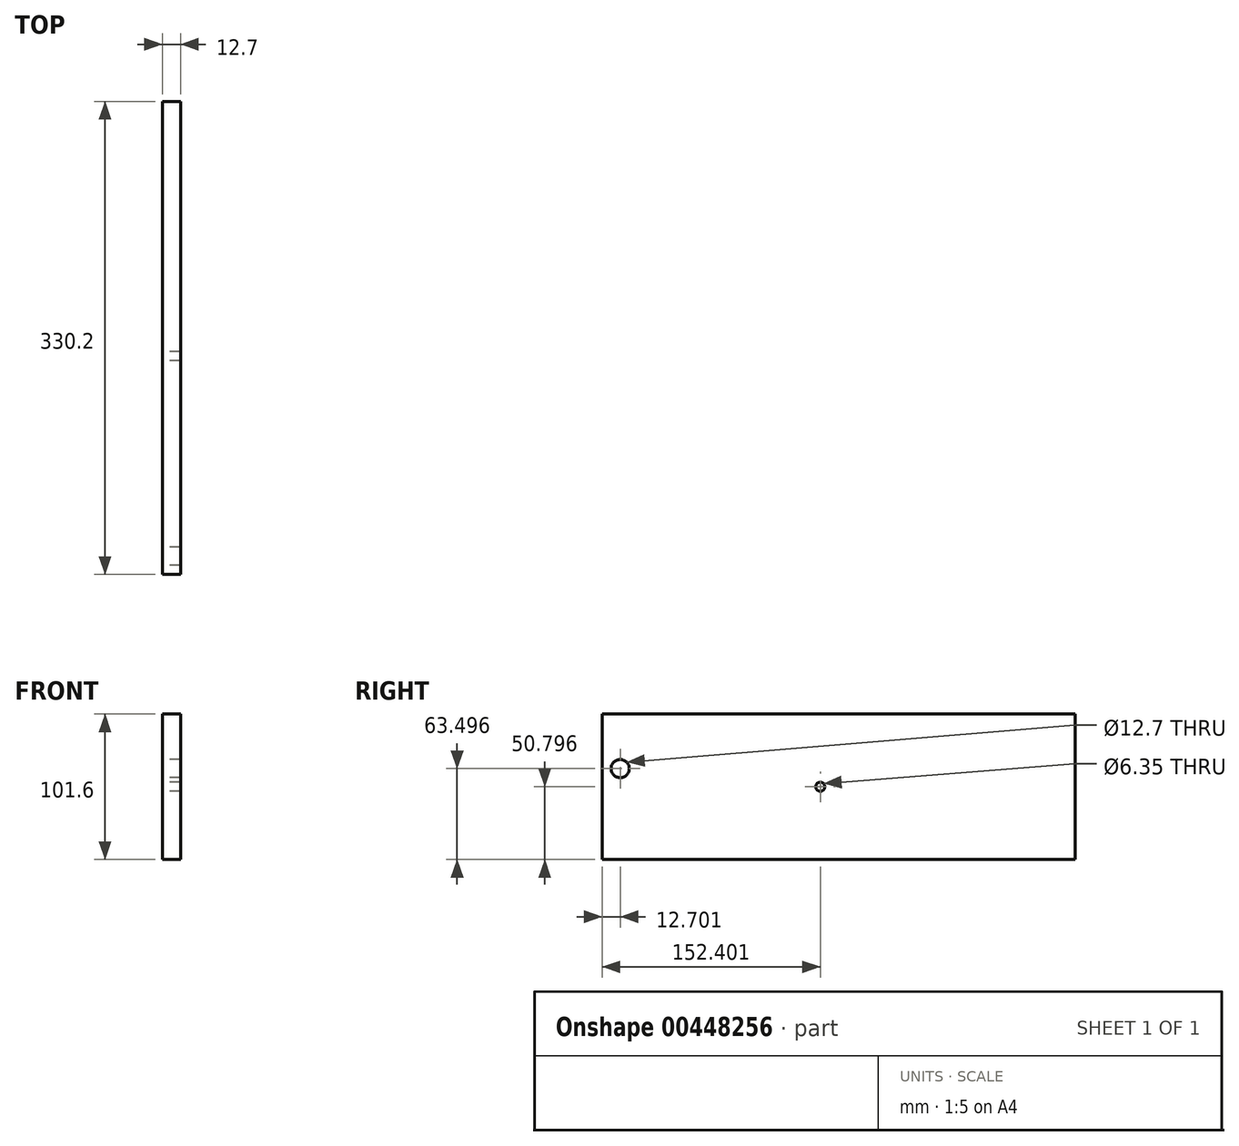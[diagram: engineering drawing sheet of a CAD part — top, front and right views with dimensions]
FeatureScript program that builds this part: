
annotation { "Feature Type Name" : "Feature", "Feature Type Description" : "" }
export const myFeature = defineFeature(function(context is Context, id is Id, definition is map)
    precondition{}
    {
        {
            var Q0;
            Q0=qCreatedBy(makeId("Right.planeOp"),FACE);
            var sketch = newSketch(context, id + "F0", { "sketchPlane" : qUnion([Q0])});
            skLineSegment(sketch, "E0.bottom", {"start": v(-112.69, 64.52) * mm, "end": v(217.51, 64.52) * mm});
            skLineSegment(sketch, "E0.top", {"start": v(-112.69, -37.08) * mm, "end": v(217.51, -37.08) * mm});
            skLineSegment(sketch, "E0.left", {"start": v(-112.69, 64.52) * mm, "end": v(-112.69, -37.08) * mm});
            skLineSegment(sketch, "E0.right", {"start": v(217.51, 64.52) * mm, "end": v(217.51, -37.08) * mm});
            skCircle(sketch, "E1", {"center": v(-99.99, 26.42) * mm, "radius": 6.35 * mm});
            skCircle(sketch, "E2", {"center": v(39.71, 13.72) * mm, "radius": 3.18 * mm});
            skSolve(sketch);
        }
        {
            var Q0;
            Q0=makeQuery(id+"F0.imprint","IMPRINT",FACE,{"disambiguationData":[TD([[makeQuery(id+"F0.imprint","IMPRINT",EDGE,{"derivedFrom":sQuery(id+"F0.wireOp",EDGE,"E0.bottom")}),-1.0]])]});
            extrude(context, id + "F1", {"entities" : qUnion([Q0]), "depth" : 12.7 * mm});
        }
    });
